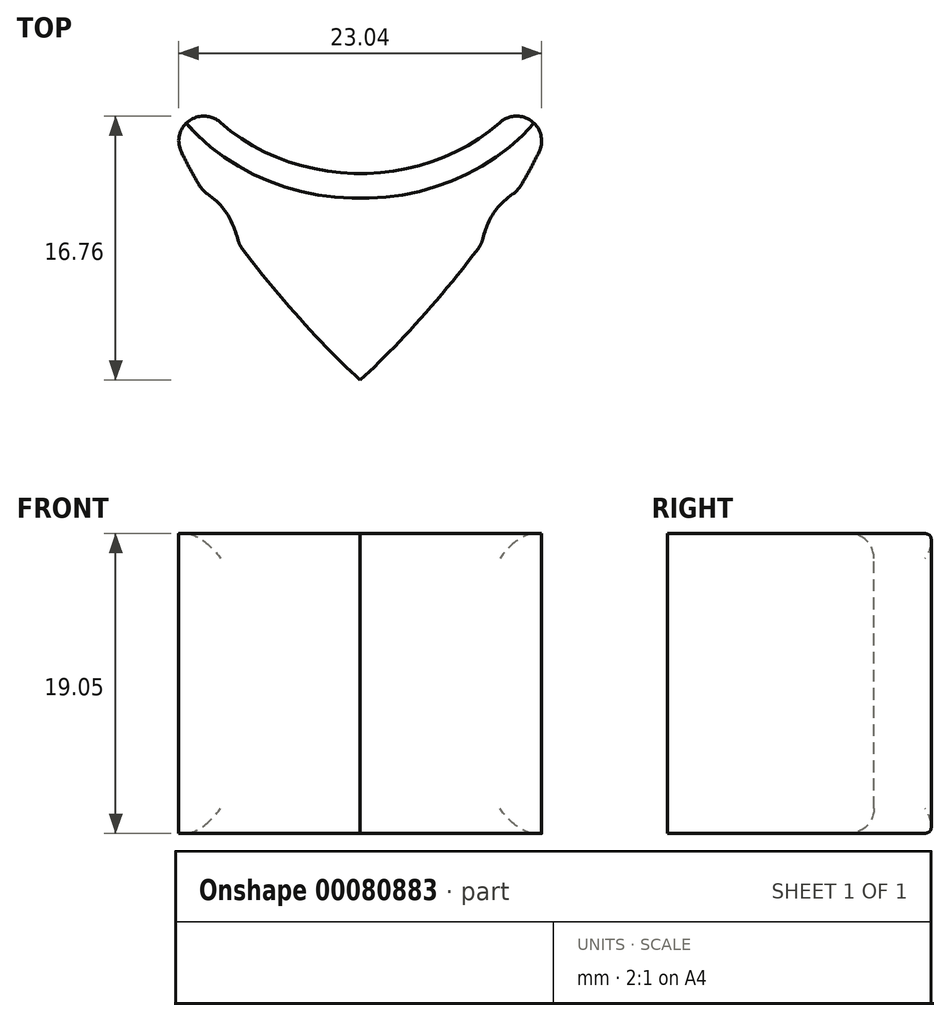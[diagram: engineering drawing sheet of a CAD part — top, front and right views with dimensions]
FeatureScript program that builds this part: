
annotation { "Feature Type Name" : "Feature", "Feature Type Description" : "" }
export const myFeature = defineFeature(function(context is Context, id is Id, definition is map)
    precondition{}
    {
        {
            var Q0;
            Q0=qCreatedBy(makeId("Top.planeOp"),FACE);
            var sketch = newSketch(context, id + "F0", { "sketchPlane" : qUnion([Q0])});
            skEllipse(sketch, "E0", {"center": v(0, 0) * mm, "majorRadius": 12.2 * mm, "minorRadius": 10.31 * mm, "majorAxis": v(1, 0)});
            skPoint(sketch, "E1.2.internal.snap0", {"position": v(0, 10.31) * mm});
            skPoint(sketch, "E1.3.internal.snap0", {"position": v(-12.2, 0) * mm});
            skPoint(sketch, "E1.4.internal.snap0", {"position": v(0, -10.31) * mm});
            skLineSegment(sketch, "E2", {"start": v(0, -10.31) * mm, "end": v(0, 10.31) * mm, "construction": true});
            skLineSegment(sketch, "E3", {"start": v(0, 0) * mm, "end": v(-63.5, 0) * mm, "construction": true});
            skFitSpline(sketch, "E4", {"points": [v(-12.2, 0) * mm, v(-12.2, -6.96) * mm, v(0, -23.43) * mm], "startDerivative": vector(-4.32, -13.13) * mm, "endDerivative": vector(19.5, -17.57) * mm});
            skFitSpline(sketch, "E5.MirrorCS", {"points": [v(12.2, 0) * mm, v(12.2, -6.96) * mm, v(0, -23.43) * mm], "startDerivative": vector(4.32, -13.13) * mm, "endDerivative": vector(-19.5, -17.57) * mm});
            skFitSpline(sketch, "E6", {"points": [v(-7.68, -14.83) * mm, v(-12.2, -10.5) * mm, v(-63.5, -6.96) * mm, v(-10.38, 5.41) * mm], "startDerivative": vector(-9.08, 32.74) * mm, "endDerivative": vector(196.7, 27.37) * mm});
            skFitSpline(sketch, "E7.MirrorCS", {"points": [v(7.68, -14.83) * mm, v(12.2, -10.5) * mm, v(63.5, -6.96) * mm, v(10.38, 5.41) * mm], "startDerivative": vector(9.08, 32.74) * mm, "endDerivative": vector(-196.7, 27.37) * mm});
            skLineSegment(sketch, "E8", {"start": v(0, -10.31) * mm, "end": v(0, -23.43) * mm, "construction": true});
            skSolve(sketch);
        }
        {
            var Q0;
            Q0=makeQuery(id+"F0.imprint","IMPRINT",FACE,{"disambiguationData":[TD([[makeQuery(id+"F0.imprint","IMPRINT",EDGE,{"derivedFrom":sQuery(id+"F0.wireOp",EDGE,"E4")}),1.0]])]});
            extrude(context, id + "F1", {"entities" : qUnion([Q0]), "depth" : 19.05 * mm});
        }
        {
            var Q0;
            Q0=makeQuery(id+"F1.opExtrude","CAP_EDGE",EDGE,{"disambiguationData":[OSD([sQuery(id+"F0.wireOp",EDGE,"E0")])],"isStart":false});
            var Q1;
            Q1=makeQuery(id+"F1.opExtrude","SWEPT_EDGE",EDGE,{"disambiguationData":[OSD([sQuery(id+"F0.wireOp",EDGE,"E0"),sQuery(id+"F0.wireOp",EDGE,"E6")])]});
            var Q2;
            Q2=makeQuery(id+"F1.opExtrude","SWEPT_EDGE",EDGE,{"disambiguationData":[OSD([sQuery(id+"F0.wireOp",EDGE,"E0"),sQuery(id+"F0.wireOp",EDGE,"E7.MirrorCS")])]});
            var Q3;
            Q3=makeQuery(id+"F1.opExtrude","CAP_EDGE",EDGE,{"disambiguationData":[OSD([sQuery(id+"F0.wireOp",EDGE,"E0")])],"isStart":true});
            fillet(context, id + "F2", {"entities" : qUnion([Q0, Q1, Q2, Q3]), "radius" : 1.59 * mm, "tangentPropagation" : true, "allowEdgeOverflow" : false});
        }
    });
